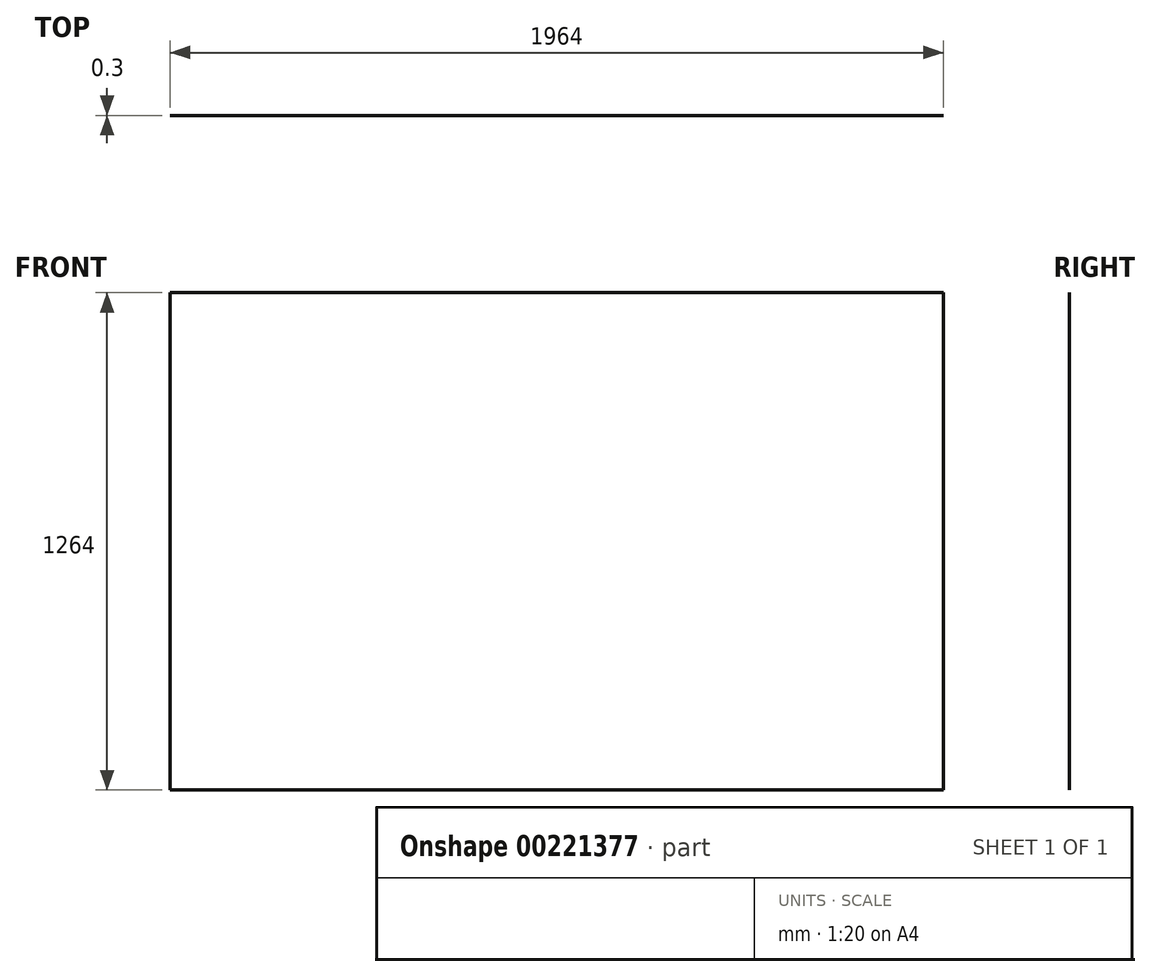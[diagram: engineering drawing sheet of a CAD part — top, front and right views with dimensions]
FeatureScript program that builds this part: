
annotation { "Feature Type Name" : "Feature", "Feature Type Description" : "" }
export const myFeature = defineFeature(function(context is Context, id is Id, definition is map)
    precondition{}
    {
        {
            var Q0;
            Q0=qCreatedBy(makeId("Front.planeOp"),FACE);
            var sketch = newSketch(context, id + "F0", { "sketchPlane" : qUnion([Q0])});
            skLineSegment(sketch, "E0.bottom", {"start": v(982, -632) * mm, "end": v(-982, -632) * mm});
            skLineSegment(sketch, "E0.top", {"start": v(982, 632) * mm, "end": v(-982, 632) * mm});
            skLineSegment(sketch, "E0.left", {"start": v(982, -632) * mm, "end": v(982, 632) * mm});
            skLineSegment(sketch, "E0.right", {"start": v(-982, -632) * mm, "end": v(-982, 632) * mm});
            skPoint(sketch, "E0.middle", {"position": v(0, 0) * mm});
            skSolve(sketch);
        }
        {
            var Q0;
            Q0 = qSketchRegion(id + "F0", true);
            extrude(context, id + "F1", {"entities" : qUnion([Q0]), "depth" : 0.3 * mm});
        }
    });
